# Revit family: Ile Club-LivingDivani
name_source: partatom
category: Furniture
revit_build: Autodesk Revit 2013 (Build: 20130531_2115(x64)
units: mm (PartAtom-declared; Revit-internal decimal feet)

## types (15) — shared parameters
Largh.BraccioloDX = 27 cm
Largh.BraccioloSX = 27 cm
Manufacturer = Living Divani srl
Mat. Tessuto = Linen, Beige
Model = Ile Club
URL = www.livingdivani.it
bracciolo DX Largo_Stretto = Yes
bracciolo SX Largo_Stretto = Yes

## per-type parameters (varying)
| type | Codice Prodotto | Dist.CuscinoDalFondo | Largh.SedutaSX | LarghezzaDivano | Lunghezza Schienale | Visib.Bracciolo Destro | Visib.Bracciolo Sinistro | Visib.Schienale | Visib.Sostegno Centrale | largh.SedutaDX | mezzaLarghezzaDX | mezzaLarghezzaSX |
| Elemento 188cm con schienale 94cm | 2ILE18894 | 0 cm | 94 cm | 188 cm | 94 cm | No | No | Yes | Yes | 94 cm | 67 cm | 67 cm |
| Centrale 188cm | 2ILE188 | 27 cm | 94 cm | 188 cm | 188 cm | No | No | Yes | Yes | 94 cm | 67 cm | 67 cm |
| Centrale 215cm | 2ILE215 | 27 cm | 108 cm | 215 cm | 215 cm | No | No | Yes | Yes | 108 cm | 81 cm | 81 cm |
| Centrale 250cm | 2ILE250 | 27 cm | 125 cm | 250 cm | 250 cm | No | No | Yes | Yes | 125 cm | 98 cm | 98 cm |
| Terminale 188cm | 2ILT188 | 27 cm | 67 cm | 188 cm | 188 cm | No | Yes | Yes | Yes | 94 cm | 67 cm | 67 cm |
| Terminale 215cm | 2ILT215 | 27 cm | 81 cm | 215 cm | 215 cm | No | Yes | Yes | Yes | 108 cm | 81 cm | 81 cm |
| Terminale 250cm | 2ILT250 | 27 cm | 98 cm | 250 cm | 250 cm | No | Yes | Yes | Yes | 125 cm | 98 cm | 98 cm |
| Elemento 188 con bracciolo e schienale 94cm | 2ILT094 | 0 cm | 67 cm | 188 cm | 94 cm | No | Yes | Yes | Yes | 94 cm | 67 cm | 67 cm |
| Elemento 215cm con bracciolo e schienale 140cm | 2ILT215140 | 0 cm | 81 cm | 215 cm | 140 cm | No | Yes | Yes | Yes | 108 cm | 81 cm | 81 cm |
| Divano 188cm | 2ILD188 | 27 cm | 67 cm | 188 cm | 188 cm | Yes | Yes | Yes | Yes | 67 cm | 67 cm | 67 cm |
| Divano 215cm | 2ILD215 | 27 cm | 81 cm | 215 cm | 215 cm | Yes | Yes | Yes | Yes | 81 cm | 81 cm | 81 cm |
| Panca 94cm | 2ILF094 | 0 cm | 47 cm | 94 cm | 94 cm | No | No | No | No | 47 cm | 20 cm | 20 cm |
| Divano 250cm | 2ILD250 | 27 cm | 98 cm | 250 cm | 250 cm | Yes | Yes | Yes | Yes | 98 cm | 98 cm | 98 cm |
| Panca 188cm | 2ILF188 | 0 cm | 94 cm | 188 cm | 188 cm | No | No | No | Yes | 94 cm | 67 cm | 67 cm |
| Panca 215 cm | 2ILF215 | 0 cm | 108 cm | 215 cm | 215 cm | No | No | No | Yes | 108 cm | 81 cm | 81 cm |

## geometry (parser evidence)
native form markers: Blend x7
no freeform markers — native parametric forms only
